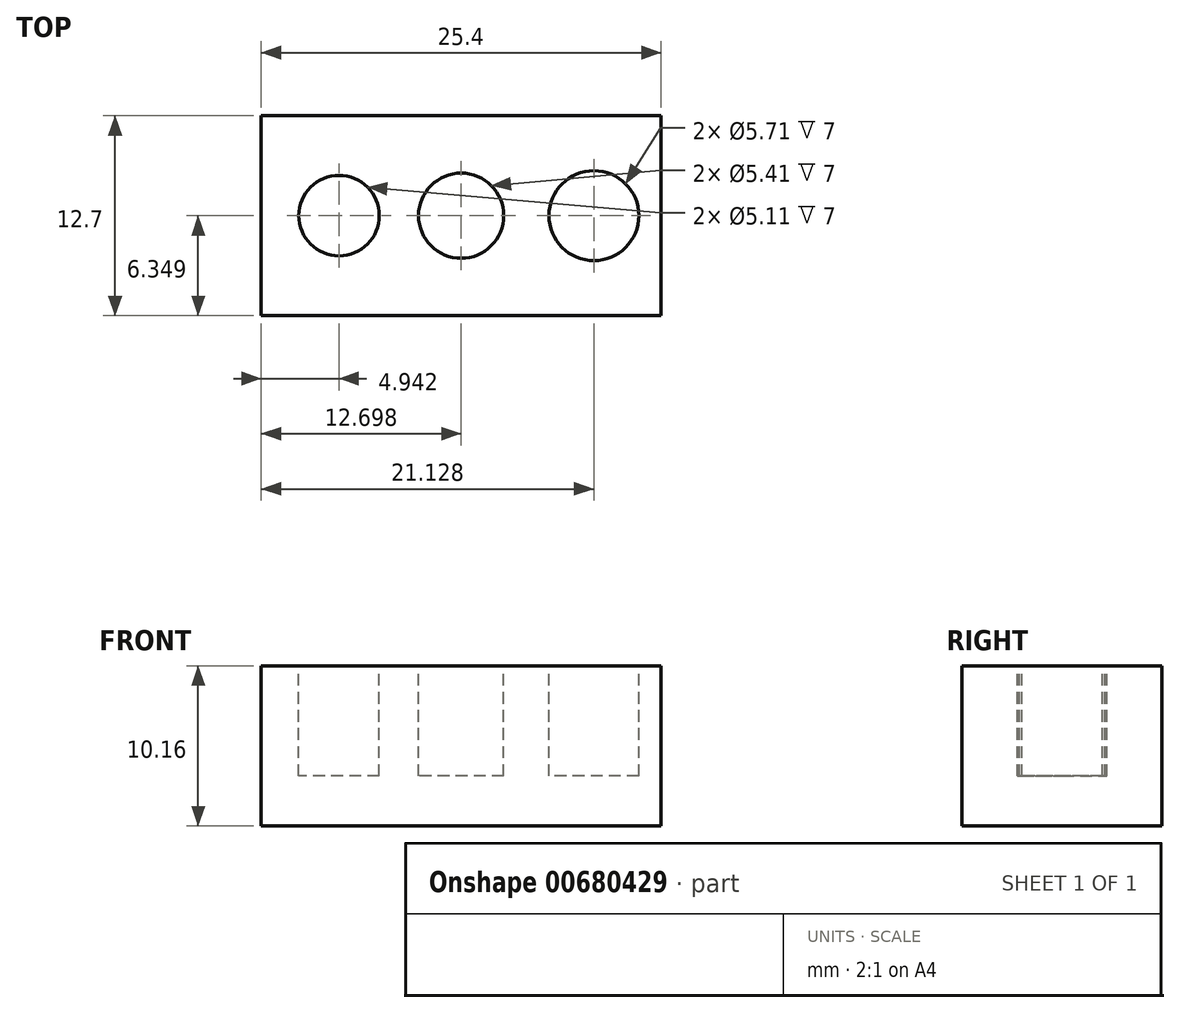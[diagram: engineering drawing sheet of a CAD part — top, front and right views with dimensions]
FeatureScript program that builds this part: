
annotation { "Feature Type Name" : "Feature", "Feature Type Description" : "" }
export const myFeature = defineFeature(function(context is Context, id is Id, definition is map)
    precondition{}
    {
        {
            var Q0;
            Q0=qCreatedBy(makeId("Top.planeOp"),FACE);
            var sketch = newSketch(context, id + "F0", { "sketchPlane" : qUnion([Q0])});
            skLineSegment(sketch, "E0.bottom", {"start": v(8.96, 1.58) * mm, "end": v(34.36, 1.58) * mm});
            skLineSegment(sketch, "E0.top", {"start": v(8.96, -11.12) * mm, "end": v(34.36, -11.12) * mm});
            skLineSegment(sketch, "E0.left", {"start": v(8.96, 1.58) * mm, "end": v(8.96, -11.12) * mm});
            skLineSegment(sketch, "E0.right", {"start": v(34.36, 1.58) * mm, "end": v(34.36, -11.12) * mm});
            skSolve(sketch);
        }
        {
            var Q0;
            Q0=makeQuery(id+"F0.imprint","IMPRINT",FACE,{"disambiguationData":[TD([[makeQuery(id+"F0.imprint","IMPRINT",EDGE,{"derivedFrom":sQuery(id+"F0.wireOp",EDGE,"E0.bottom")}),-1.0]])]});
            extrude(context, id + "F1", {"entities" : qUnion([Q0]), "depth" : 10.16 * mm, "offsetDistance" : 25.4 * mm});
        }
        {
            var Q0;
            Q0=makeQuery(id+"F1.opExtrude","CAP_FACE",FACE,{"disambiguationData":[OSD([sQuery(id+"F0.wireOp",EDGE,"E0.bottom"),sQuery(id+"F0.wireOp",EDGE,"E0.top"),sQuery(id+"F0.wireOp",EDGE,"E0.left"),sQuery(id+"F0.wireOp",EDGE,"E0.right")])],"isStart":false});
            var sketch = newSketch(context, id + "F2", { "sketchPlane" : qUnion([Q0])});
            skCircle(sketch, "E1", {"center": v(21.66, -4.77) * mm, "radius": 2.7 * mm});
            skPoint(sketch, "E1.centerSnap0", {"position": v(8.96, -4.77) * mm});
            skLineSegment(sketch, "E2", {"start": v(8.96, -4.77) * mm, "end": v(34.36, -4.77) * mm, "construction": true});
            skCircle(sketch, "E3", {"center": v(30.09, -4.77) * mm, "radius": 2.86 * mm});
            skCircle(sketch, "E4", {"center": v(13.9, -4.77) * mm, "radius": 2.56 * mm});
            skSolve(sketch);
        }
        {
            var Q0;
            Q0=makeQuery(id+"F2.imprint","IMPRINT",FACE,{"disambiguationData":[TD([[makeQuery(id+"F2.imprint","IMPRINT",EDGE,{"derivedFrom":sQuery(id+"F2.wireOp",EDGE,"E4")}),1.0]])]});
            var Q1;
            Q1=makeQuery(id+"F2.imprint","IMPRINT",FACE,{"disambiguationData":[TD([[makeQuery(id+"F2.imprint","IMPRINT",EDGE,{"derivedFrom":sQuery(id+"F2.wireOp",EDGE,"E1")}),1.0]])]});
            var Q2;
            Q2=makeQuery(id+"F2.imprint","IMPRINT",FACE,{"disambiguationData":[TD([[makeQuery(id+"F2.imprint","IMPRINT",EDGE,{"derivedFrom":sQuery(id+"F2.wireOp",EDGE,"E3")}),1.0]])]});
            extrude(context, id + "F3", {"entities" : qUnion([Q0, Q1, Q2]), "operationType" : NewBodyOperationType.REMOVE, "oppositeDirection" : true, "depth" : 7 * mm, "offsetDistance" : 25.4 * mm});
        }
    });
